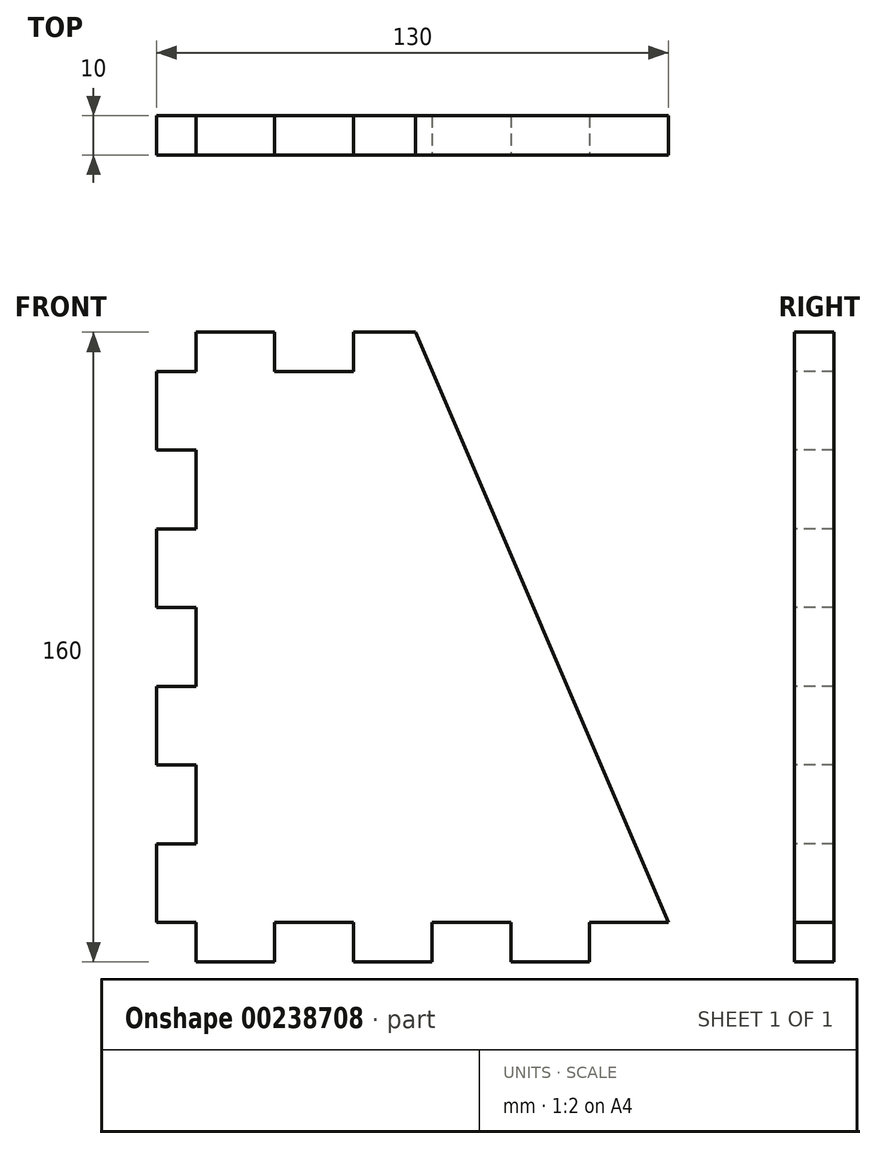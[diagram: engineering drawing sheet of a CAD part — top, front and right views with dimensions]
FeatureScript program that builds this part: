
annotation { "Feature Type Name" : "Feature", "Feature Type Description" : "" }
export const myFeature = defineFeature(function(context is Context, id is Id, definition is map)
    precondition{}
    {
        {
            var Q0;
            Q0=qCreatedBy(makeId("Front.planeOp"),FACE);
            var sketch = newSketch(context, id + "F0", { "sketchPlane" : qUnion([Q0])});
            skLineSegment(sketch, "E0.bottom", {"start": v(0, -100) * mm, "end": v(250, -100) * mm, "construction": true});
            skLineSegment(sketch, "E0.top", {"start": v(0, 40) * mm, "end": v(250, 40) * mm, "construction": true});
            skLineSegment(sketch, "E0.right", {"start": v(250, -100) * mm, "end": v(250, 40) * mm, "construction": true});
            skLineSegment(sketch, "E1", {"start": v(125, -92.5) * mm, "end": v(125, -100) * mm, "construction": true});
            skLineSegment(sketch, "E2.top", {"start": v(135, -110) * mm, "end": v(115, -110) * mm});
            skLineSegment(sketch, "E2.left", {"start": v(135, -100) * mm, "end": v(135, -110) * mm});
            skLineSegment(sketch, "E2.right", {"start": v(115, -100) * mm, "end": v(115, -110) * mm});
            skPoint(sketch, "E2.middle", {"position": v(125, -105) * mm});
            skLineSegment(sketch, "E3", {"start": v(135, -100) * mm, "end": v(155, -100) * mm});
            skLineSegment(sketch, "E4.1.0.0", {"start": v(155, -100) * mm, "end": v(155, -110) * mm});
            skLineSegment(sketch, "E4.1.0.1", {"start": v(175, -110) * mm, "end": v(155, -110) * mm});
            skLineSegment(sketch, "E4.1.0.2", {"start": v(175, -100) * mm, "end": v(175, -110) * mm});
            skLineSegment(sketch, "E4.1.0.3", {"start": v(175, -100) * mm, "end": v(195, -100) * mm});
            skLineSegment(sketch, "E4.2.0.0", {"start": v(195, -100) * mm, "end": v(195, -110) * mm});
            skLineSegment(sketch, "E4.2.0.1", {"start": v(215, -110) * mm, "end": v(195, -110) * mm});
            skLineSegment(sketch, "E4.2.0.2", {"start": v(215, -100) * mm, "end": v(215, -110) * mm});
            skLineSegment(sketch, "E4.2.0.3", {"start": v(215, -100) * mm, "end": v(235, -100) * mm});
            skLineSegment(sketch, "E4.direction1", {"start": v(115, -110) * mm, "end": v(155, -110) * mm, "construction": true});
            skLineSegment(sketch, "E5.0.3.0", {"start": v(235, -100) * mm, "end": v(235, -110) * mm});
            skLineSegment(sketch, "E6.MirrorCS", {"start": v(15, -100) * mm, "end": v(15, -110) * mm});
            skLineSegment(sketch, "E7.MirrorCS", {"start": v(35, -100) * mm, "end": v(35, -110) * mm});
            skLineSegment(sketch, "E8.MirrorCS", {"start": v(35, -110) * mm, "end": v(55, -110) * mm});
            skLineSegment(sketch, "E9.MirrorCS", {"start": v(55, -100) * mm, "end": v(55, -110) * mm});
            skLineSegment(sketch, "E10.MirrorCS", {"start": v(75, -100) * mm, "end": v(75, -110) * mm});
            skLineSegment(sketch, "E11.MirrorCS", {"start": v(75, -110) * mm, "end": v(95, -110) * mm});
            skLineSegment(sketch, "E12.MirrorCS", {"start": v(95, -100) * mm, "end": v(95, -110) * mm});
            skLineSegment(sketch, "E13.MirrorCS", {"start": v(35, -100) * mm, "end": v(15, -100) * mm});
            skLineSegment(sketch, "E14.MirrorCS", {"start": v(115, -100) * mm, "end": v(95, -100) * mm});
            skLineSegment(sketch, "E15.MirrorCS", {"start": v(75, -100) * mm, "end": v(55, -100) * mm});
            skLineSegment(sketch, "E16.bottom", {"start": v(250, -20) * mm, "end": v(260, -20) * mm});
            skLineSegment(sketch, "E16.top", {"start": v(250, -40) * mm, "end": v(260, -40) * mm});
            skLineSegment(sketch, "E16.right", {"start": v(260, -20) * mm, "end": v(260, -40) * mm});
            skPoint(sketch, "E16.middle", {"position": v(255, -30) * mm});
            skPoint(sketch, "E16.middle.positionSnap0", {"position": v(250, -30) * mm});
            skPoint(sketch, "E16.centerSnap0", {"position": v(250, -30) * mm});
            skLineSegment(sketch, "E17", {"start": v(250, -20) * mm, "end": v(250, 0) * mm});
            skLineSegment(sketch, "E18.0.1.0", {"start": v(250, 0) * mm, "end": v(260, 0) * mm});
            skLineSegment(sketch, "E18.0.1.1", {"start": v(260, 20) * mm, "end": v(260, 0) * mm});
            skLineSegment(sketch, "E18.0.1.2", {"start": v(250, 20) * mm, "end": v(260, 20) * mm});
            skLineSegment(sketch, "E18.0.1.3", {"start": v(250, 20) * mm, "end": v(250, 40) * mm});
            skLineSegment(sketch, "E18.0.2.0", {"start": v(250, 40) * mm, "end": v(260, 40) * mm});
            skLineSegment(sketch, "E18.direction1", {"start": v(250, -40) * mm, "end": v(275, -40) * mm, "construction": true});
            skLineSegment(sketch, "E18.direction2", {"start": v(250, -40) * mm, "end": v(250, 0) * mm, "construction": true});
            skLineSegment(sketch, "E19", {"start": v(255, -30) * mm, "end": v(250, -30) * mm, "construction": true});
            skLineSegment(sketch, "E20.MirrorCS", {"start": v(250, -40) * mm, "end": v(250, -60) * mm});
            skLineSegment(sketch, "E21.MirrorCS", {"start": v(250, -60) * mm, "end": v(260, -60) * mm});
            skLineSegment(sketch, "E22.MirrorCS", {"start": v(260, -80) * mm, "end": v(260, -60) * mm});
            skLineSegment(sketch, "E23.MirrorCS", {"start": v(250, -80) * mm, "end": v(260, -80) * mm});
            skLineSegment(sketch, "E24.MirrorCS", {"start": v(250, -80) * mm, "end": v(250, -100) * mm});
            skLineSegment(sketch, "E25.MirrorCS", {"start": v(250, -100) * mm, "end": v(260, -100) * mm});
            skLineSegment(sketch, "E26", {"start": v(235, -110) * mm, "end": v(260, -110) * mm});
            skLineSegment(sketch, "E27", {"start": v(260, -110) * mm, "end": v(260, -100) * mm});
            skLineSegment(sketch, "E28.MirrorCS", {"start": v(35, 40) * mm, "end": v(35, 50) * mm});
            skLineSegment(sketch, "E29.MirrorCS", {"start": v(115, 40) * mm, "end": v(115, 50) * mm});
            skLineSegment(sketch, "E30.MirrorCS", {"start": v(55, 40) * mm, "end": v(55, 50) * mm});
            skLineSegment(sketch, "E31.MirrorCS", {"start": v(155, 40) * mm, "end": v(155, 50) * mm});
            skLineSegment(sketch, "E32.MirrorCS", {"start": v(75, 40) * mm, "end": v(75, 50) * mm});
            skLineSegment(sketch, "E33.MirrorCS", {"start": v(235, 40) * mm, "end": v(235, 50) * mm});
            skLineSegment(sketch, "E34.MirrorCS", {"start": v(95, 40) * mm, "end": v(95, 50) * mm});
            skLineSegment(sketch, "E35.MirrorCS", {"start": v(15, 40) * mm, "end": v(15, 50) * mm});
            skLineSegment(sketch, "E36.MirrorCS", {"start": v(260, 50) * mm, "end": v(260, 40) * mm});
            skLineSegment(sketch, "E37.MirrorCS", {"start": v(175, 40) * mm, "end": v(175, 50) * mm});
            skLineSegment(sketch, "E38.MirrorCS", {"start": v(195, 40) * mm, "end": v(195, 50) * mm});
            skLineSegment(sketch, "E39.MirrorCS", {"start": v(135, 40) * mm, "end": v(135, 50) * mm});
            skLineSegment(sketch, "E40.MirrorCS", {"start": v(215, 40) * mm, "end": v(215, 50) * mm});
            skLineSegment(sketch, "E41.MirrorCS", {"start": v(135, 40) * mm, "end": v(155, 40) * mm});
            skLineSegment(sketch, "E42.MirrorCS", {"start": v(215, 40) * mm, "end": v(235, 40) * mm});
            skLineSegment(sketch, "E43.MirrorCS", {"start": v(175, 40) * mm, "end": v(195, 40) * mm});
            skLineSegment(sketch, "E44.MirrorCS", {"start": v(35, 40) * mm, "end": v(15, 40) * mm});
            skLineSegment(sketch, "E45.MirrorCS", {"start": v(115, 40) * mm, "end": v(95, 40) * mm});
            skLineSegment(sketch, "E46.MirrorCS", {"start": v(75, 40) * mm, "end": v(55, 40) * mm});
            skLineSegment(sketch, "E47.MirrorCS", {"start": v(135, 50) * mm, "end": v(115, 50) * mm});
            skLineSegment(sketch, "E48.MirrorCS", {"start": v(35, 50) * mm, "end": v(55, 50) * mm});
            skLineSegment(sketch, "E49.MirrorCS", {"start": v(175, 50) * mm, "end": v(155, 50) * mm});
            skLineSegment(sketch, "E50.MirrorCS", {"start": v(215, 50) * mm, "end": v(195, 50) * mm});
            skLineSegment(sketch, "E51.MirrorCS", {"start": v(75, 50) * mm, "end": v(95, 50) * mm});
            skLineSegment(sketch, "E52.MirrorCS", {"start": v(235, 50) * mm, "end": v(260, 50) * mm});
            skLineSegment(sketch, "E53.MirrorCS", {"start": v(15, -110) * mm, "end": v(-10, -110) * mm});
            skLineSegment(sketch, "E54.MirrorCS", {"start": v(-10, -110) * mm, "end": v(-10, -100) * mm});
            skLineSegment(sketch, "E55.MirrorCS", {"start": v(0, -100) * mm, "end": v(-10, -100) * mm});
            skLineSegment(sketch, "E56.MirrorCS", {"start": v(0, -80) * mm, "end": v(-10, -80) * mm});
            skLineSegment(sketch, "E57.MirrorCS", {"start": v(-10, -80) * mm, "end": v(-10, -60) * mm});
            skLineSegment(sketch, "E58.MirrorCS", {"start": v(0, -60) * mm, "end": v(-10, -60) * mm});
            skLineSegment(sketch, "E59.MirrorCS", {"start": v(0, -100) * mm, "end": v(0, 40) * mm, "construction": true});
            skLineSegment(sketch, "E60.MirrorCS", {"start": v(-10, -20) * mm, "end": v(-10, -40) * mm, "construction": true});
            skLineSegment(sketch, "E61.MirrorCS", {"start": v(0, -20) * mm, "end": v(-10, -20) * mm});
            skLineSegment(sketch, "E62.MirrorCS", {"start": v(0, 0) * mm, "end": v(-10, 0) * mm});
            skLineSegment(sketch, "E63.MirrorCS", {"start": v(-10, 20) * mm, "end": v(-10, 0) * mm});
            skLineSegment(sketch, "E64.MirrorCS", {"start": v(0, 20) * mm, "end": v(-10, 20) * mm});
            skLineSegment(sketch, "E65.MirrorCS", {"start": v(0, 40) * mm, "end": v(-10, 40) * mm});
            skLineSegment(sketch, "E66.MirrorCS", {"start": v(-10, 50) * mm, "end": v(-10, 40) * mm});
            skLineSegment(sketch, "E67.MirrorCS", {"start": v(0, 20) * mm, "end": v(0, 40) * mm});
            skLineSegment(sketch, "E68.MirrorCS", {"start": v(0, -20) * mm, "end": v(0, 0) * mm});
            skLineSegment(sketch, "E69.MirrorCS", {"start": v(0, -40) * mm, "end": v(0, -60) * mm});
            skLineSegment(sketch, "E70.MirrorCS", {"start": v(0, -80) * mm, "end": v(0, -100) * mm});
            skLineSegment(sketch, "E71.MirrorCS", {"start": v(0, -40) * mm, "end": v(-10, -40) * mm});
            skLineSegment(sketch, "E72", {"start": v(-10, 50) * mm, "end": v(15, 50) * mm});
            skLineSegment(sketch, "E73.bottom", {"start": v(-10, -110) * mm, "end": v(260, -110) * mm, "construction": true});
            skLineSegment(sketch, "E73.top", {"start": v(-10, -230) * mm, "end": v(260, -230) * mm});
            skLineSegment(sketch, "E73.left", {"start": v(-10, -110) * mm, "end": v(-10, -230) * mm, "construction": true});
            skLineSegment(sketch, "E73.right", {"start": v(260, -110) * mm, "end": v(260, -230) * mm, "construction": true});
            skLineSegment(sketch, "E74.bottom", {"start": v(260, 50) * mm, "end": v(-10, 50) * mm, "construction": true});
            skLineSegment(sketch, "E74.top", {"start": v(260, 110) * mm, "end": v(-10, 110) * mm});
            skLineSegment(sketch, "E74.left", {"start": v(260, 50) * mm, "end": v(260, 110) * mm, "construction": true});
            skLineSegment(sketch, "E74.right", {"start": v(-10, 50) * mm, "end": v(-10, 110) * mm, "construction": true});
            skLineSegment(sketch, "E75.bottom", {"start": v(260, 40) * mm, "end": v(320, 40) * mm, "construction": true});
            skLineSegment(sketch, "E75.top", {"start": v(260, -100) * mm, "end": v(380, -100) * mm, "construction": true});
            skLineSegment(sketch, "E75.right", {"start": v(320, 40) * mm, "end": v(380, -100) * mm});
            skLineSegment(sketch, "E76.top", {"start": v(260, -110) * mm, "end": v(280, -110) * mm});
            skLineSegment(sketch, "E76.left", {"start": v(260, -100) * mm, "end": v(260, -110) * mm});
            skLineSegment(sketch, "E76.right", {"start": v(280, -100) * mm, "end": v(280, -110) * mm});
            skLineSegment(sketch, "E77", {"start": v(280, -100) * mm, "end": v(300, -100) * mm});
            skLineSegment(sketch, "E78.1.0.0", {"start": v(320, -100) * mm, "end": v(340, -100) * mm});
            skLineSegment(sketch, "E78.1.0.1", {"start": v(320, -100) * mm, "end": v(320, -110) * mm});
            skLineSegment(sketch, "E78.1.0.2", {"start": v(300, -110) * mm, "end": v(320, -110) * mm});
            skLineSegment(sketch, "E78.1.0.3", {"start": v(300, -100) * mm, "end": v(300, -110) * mm});
            skLineSegment(sketch, "E78.2.0.0", {"start": v(360, -100) * mm, "end": v(380, -100) * mm});
            skLineSegment(sketch, "E78.2.0.1", {"start": v(360, -100) * mm, "end": v(360, -110) * mm});
            skLineSegment(sketch, "E78.2.0.2", {"start": v(340, -110) * mm, "end": v(360, -110) * mm});
            skLineSegment(sketch, "E78.2.0.3", {"start": v(340, -100) * mm, "end": v(340, -110) * mm});
            skLineSegment(sketch, "E78.direction1", {"start": v(260, -110) * mm, "end": v(300, -110) * mm, "construction": true});
            skLineSegment(sketch, "E79.top", {"start": v(250, -110) * mm, "end": v(250, -130) * mm});
            skLineSegment(sketch, "E79.left", {"start": v(260, -110) * mm, "end": v(250, -110) * mm});
            skLineSegment(sketch, "E79.right", {"start": v(260, -130) * mm, "end": v(250, -130) * mm});
            skLineSegment(sketch, "E80", {"start": v(260, -130) * mm, "end": v(260, -150) * mm});
            skLineSegment(sketch, "E81.1.0.0", {"start": v(260, -170) * mm, "end": v(260, -190) * mm});
            skLineSegment(sketch, "E81.1.0.1", {"start": v(260, -170) * mm, "end": v(250, -170) * mm});
            skLineSegment(sketch, "E81.1.0.2", {"start": v(250, -150) * mm, "end": v(250, -170) * mm});
            skLineSegment(sketch, "E81.1.0.3", {"start": v(260, -150) * mm, "end": v(250, -150) * mm});
            skLineSegment(sketch, "E81.2.0.0", {"start": v(260, -210) * mm, "end": v(260, -230) * mm});
            skLineSegment(sketch, "E81.2.0.1", {"start": v(260, -210) * mm, "end": v(250, -210) * mm});
            skLineSegment(sketch, "E81.2.0.2", {"start": v(250, -190) * mm, "end": v(250, -210) * mm});
            skLineSegment(sketch, "E81.2.0.3", {"start": v(260, -190) * mm, "end": v(250, -190) * mm});
            skLineSegment(sketch, "E81.direction1", {"start": v(250, -110) * mm, "end": v(250, -150) * mm, "construction": true});
            skLineSegment(sketch, "E82.MirrorCS", {"start": v(280, 40) * mm, "end": v(280, 50) * mm});
            skLineSegment(sketch, "E83.MirrorCS", {"start": v(280, 40) * mm, "end": v(300, 40) * mm});
            skLineSegment(sketch, "E84.MirrorCS", {"start": v(300, 40) * mm, "end": v(300, 50) * mm});
            skLineSegment(sketch, "E85.MirrorCS", {"start": v(300, 50) * mm, "end": v(320, 50) * mm});
            skLineSegment(sketch, "E86.MirrorCS", {"start": v(320, 40) * mm, "end": v(320, 50) * mm, "construction": true});
            skLineSegment(sketch, "E87.MirrorCS", {"start": v(260, 40) * mm, "end": v(260, 50) * mm});
            skLineSegment(sketch, "E88.MirrorCS", {"start": v(260, 50) * mm, "end": v(280, 50) * mm});
            skLineSegment(sketch, "E89.MirrorCS", {"start": v(250, 50) * mm, "end": v(250, 70) * mm});
            skLineSegment(sketch, "E90.MirrorCS", {"start": v(260, 70) * mm, "end": v(250, 70) * mm});
            skLineSegment(sketch, "E91.MirrorCS", {"start": v(260, 70) * mm, "end": v(260, 90) * mm});
            skLineSegment(sketch, "E92.MirrorCS", {"start": v(260, 90) * mm, "end": v(250, 90) * mm});
            skLineSegment(sketch, "E93.MirrorCS", {"start": v(250, 90) * mm, "end": v(250, 110) * mm});
            skLineSegment(sketch, "E94.MirrorCS", {"start": v(-10, -210) * mm, "end": v(-10, -230) * mm});
            skLineSegment(sketch, "E95.MirrorCS", {"start": v(-10, -210) * mm, "end": v(0, -210) * mm});
            skLineSegment(sketch, "E96.MirrorCS", {"start": v(0, -190) * mm, "end": v(0, -210) * mm});
            skLineSegment(sketch, "E97.MirrorCS", {"start": v(-10, -190) * mm, "end": v(0, -190) * mm});
            skLineSegment(sketch, "E98.MirrorCS", {"start": v(-10, -170) * mm, "end": v(-10, -190) * mm});
            skLineSegment(sketch, "E99.MirrorCS", {"start": v(-10, -170) * mm, "end": v(0, -170) * mm});
            skLineSegment(sketch, "E100.MirrorCS", {"start": v(0, -150) * mm, "end": v(0, -170) * mm});
            skLineSegment(sketch, "E101.MirrorCS", {"start": v(-10, -150) * mm, "end": v(0, -150) * mm});
            skLineSegment(sketch, "E102.MirrorCS", {"start": v(-10, -130) * mm, "end": v(-10, -150) * mm});
            skLineSegment(sketch, "E103.MirrorCS", {"start": v(-10, -130) * mm, "end": v(0, -130) * mm});
            skLineSegment(sketch, "E104.MirrorCS", {"start": v(0, -110) * mm, "end": v(0, -150) * mm, "construction": true});
            skLineSegment(sketch, "E105.MirrorCS", {"start": v(0, -110) * mm, "end": v(0, -130) * mm});
            skLineSegment(sketch, "E106.MirrorCS", {"start": v(0, 50) * mm, "end": v(0, 70) * mm});
            skLineSegment(sketch, "E107.MirrorCS", {"start": v(-10, 70) * mm, "end": v(0, 70) * mm});
            skLineSegment(sketch, "E108.MirrorCS", {"start": v(-10, 70) * mm, "end": v(-10, 90) * mm});
            skLineSegment(sketch, "E109.MirrorCS", {"start": v(-10, 90) * mm, "end": v(0, 90) * mm});
            skLineSegment(sketch, "E110.MirrorCS", {"start": v(0, 90) * mm, "end": v(0, 110) * mm});
            skLineSegment(sketch, "E111", {"start": v(320, 40) * mm, "end": v(315.71, 50) * mm});
            skSolve(sketch);
        }
        {
            var Q0;
            Q0=makeQuery(id+"F0.imprint","IMPRINT",FACE,{"disambiguationData":[TD([[makeQuery(id+"F0.imprint","IMPRINT",EDGE,{"derivedFrom":sQuery(id+"F0.wireOp",EDGE,"6DD6EAd9-EjR4-M54x-3Gs5-ZzkpjLEBHBt8.bottom")}),1.0]])]});
            var Q1;
            Q1=makeQuery(id+"F0.imprint","IMPRINT",FACE,{"disambiguationData":[TD([[makeQuery(id+"F0.imprint","IMPRINT",EDGE,{"derivedFrom":sQuery(id+"F0.wireOp",EDGE,"3aa721ca-eb7f-4933-b860-b67e4f9833b7.bottom")}),1.0]])]});
            var Q2;
            Q2=makeQuery(id+"F0.imprint","IMPRINT",FACE,{"disambiguationData":[TD([[makeQuery(id+"F0.imprint","IMPRINT",EDGE,{"derivedFrom":sQuery(id+"F0.wireOp",EDGE,"1f1aca45-ddc4-4c07-b0ce-2f99aba2689f.bottom")}),1.0]])]});
            var Q3;
            Q3=makeQuery(id+"F0.imprint","IMPRINT",FACE,{"disambiguationData":[TD([[makeQuery(id+"F0.imprint","IMPRINT",EDGE,{"derivedFrom":sQuery(id+"F0.wireOp",EDGE,"cb640f68-ba69-4848-84fb-c352f3b5514c.1.0.0")}),-1.0]])]});
            var Q4;
            Q4=makeQuery(id+"F0.imprint","IMPRINT",FACE,{"disambiguationData":[TD([[makeQuery(id+"F0.imprint","IMPRINT",EDGE,{"derivedFrom":sQuery(id+"F0.wireOp",EDGE,"be0e698b-39bb-4470-8cd3-9eb53d7fa9ec.3.0.4")}),-1.0]])]});
            var Q5;
            Q5=makeQuery(id+"F0.imprint","IMPRINT",FACE,{"disambiguationData":[TD([[makeQuery(id+"F0.imprint","IMPRINT",EDGE,{"derivedFrom":sQuery(id+"F0.wireOp",EDGE,"be0e698b-39bb-4470-8cd3-9eb53d7fa9ec.2.0.4")}),-1.0]])]});
            var Q6;
            Q6=makeQuery(id+"F0.imprint","IMPRINT",FACE,{"disambiguationData":[TD([[makeQuery(id+"F0.imprint","IMPRINT",EDGE,{"derivedFrom":sQuery(id+"F0.wireOp",EDGE,"be0e698b-39bb-4470-8cd3-9eb53d7fa9ec.1.0.4")}),-1.0]])]});
            var Q7;
            Q7=makeQuery(id+"F0.imprint","IMPRINT",FACE,{"disambiguationData":[TD([[makeQuery(id+"F0.imprint","IMPRINT",EDGE,{"derivedFrom":sQuery(id+"F0.wireOp",EDGE,"KLXXNCfZ-N2lI-LQPs-WN5Q-R0OJi47yWmJK")}),-1.0]])]});
            var Q8;
            Q8=makeQuery(id+"F0.imprint","IMPRINT",FACE,{"disambiguationData":[TD([[makeQuery(id+"F0.imprint","IMPRINT",EDGE,{"derivedFrom":sQuery(id+"F0.wireOp",EDGE,"E16.bottom")}),1.0]])]});
            extrude(context, id + "F1", {"entities" : qUnion([Q0, Q1, Q2, Q3, Q4, Q5, Q6, Q7, Q8]), "oppositeDirection" : true, "depth" : 10 * mm});
        }
    });
